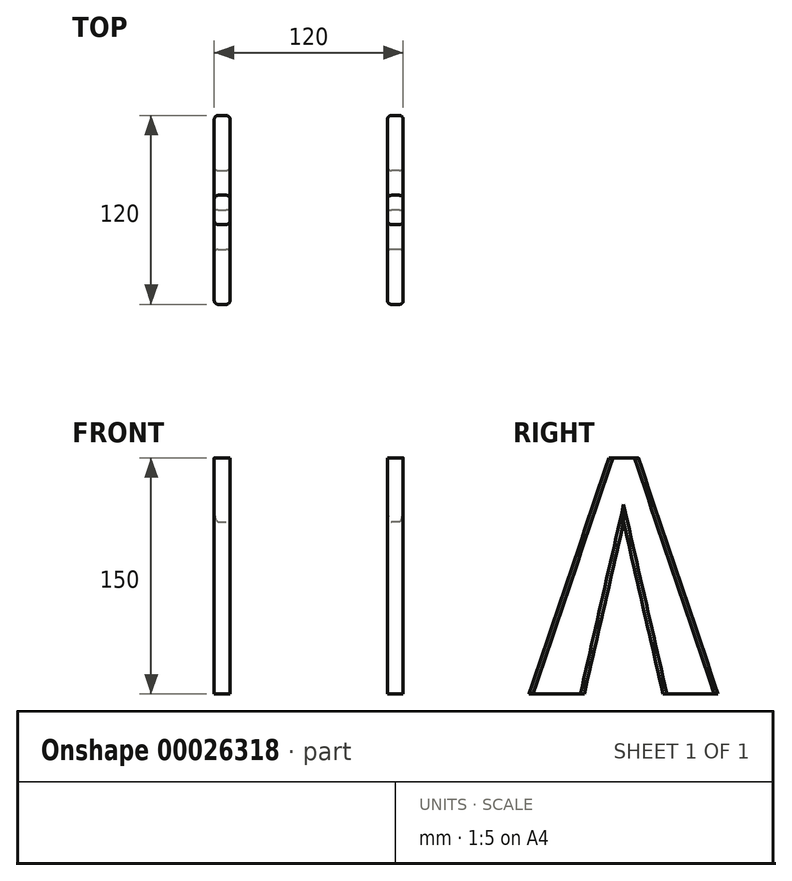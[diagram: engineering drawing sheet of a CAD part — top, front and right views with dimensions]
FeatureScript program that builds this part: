
annotation { "Feature Type Name" : "Feature", "Feature Type Description" : "" }
export const myFeature = defineFeature(function(context is Context, id is Id, definition is map)
    precondition{}
    {
        {
            var Q0;
            Q0=qCreatedBy(makeId("Top.planeOp"),FACE);
            var sketch = newSketch(context, id + "F0", { "sketchPlane" : qUnion([Q0])});
            skLineSegment(sketch, "E0.bottom", {"start": v(-57.5, -25) * mm, "end": v(-52.5, -25) * mm});
            skLineSegment(sketch, "E0.top", {"start": v(-57.5, -60) * mm, "end": v(-52.5, -60) * mm});
            skLineSegment(sketch, "E0.left", {"start": v(-60, -27.5) * mm, "end": v(-60, -57.5) * mm});
            skLineSegment(sketch, "E0.right", {"start": v(-50, -27.5) * mm, "end": v(-50, -57.5) * mm});
            skLineSegment(sketch, "E1.MirrorCS", {"start": v(-57.5, 25) * mm, "end": v(-52.5, 25) * mm});
            skLineSegment(sketch, "E2.MirrorCS", {"start": v(-57.5, 60) * mm, "end": v(-52.5, 60) * mm});
            skLineSegment(sketch, "E3.MirrorCS", {"start": v(-50, 27.5) * mm, "end": v(-50, 57.5) * mm});
            skLineSegment(sketch, "E4.MirrorCS", {"start": v(-60, 27.5) * mm, "end": v(-60, 57.5) * mm});
            skPoint(sketch, "E5.visualSharp", {"position": v(-60, -60) * mm});
            skArc(sketch, "E5.filletArc", {"start": v(-60, -57.5) * mm, "mid": v(-59.27, -59.27) * mm, "end": v(-57.5, -60) * mm});
            skPoint(sketch, "E6.visualSharp", {"position": v(-50, -25) * mm});
            skArc(sketch, "E6.filletArc", {"start": v(-50, -27.5) * mm, "mid": v(-50.73, -25.73) * mm, "end": v(-52.5, -25) * mm});
            skPoint(sketch, "E7.visualSharp", {"position": v(-60, -25) * mm});
            skArc(sketch, "E7.filletArc", {"start": v(-57.5, -25) * mm, "mid": v(-59.27, -25.73) * mm, "end": v(-60, -27.5) * mm});
            skPoint(sketch, "E8.visualSharp", {"position": v(-50, -60) * mm});
            skArc(sketch, "E8.filletArc", {"start": v(-52.5, -60) * mm, "mid": v(-50.73, -59.27) * mm, "end": v(-50, -57.5) * mm});
            skPoint(sketch, "E9.visualSharp", {"position": v(-50, 25) * mm});
            skArc(sketch, "E9.filletArc", {"start": v(-52.5, 25) * mm, "mid": v(-50.73, 25.73) * mm, "end": v(-50, 27.5) * mm});
            skPoint(sketch, "E10.visualSharp", {"position": v(-60, 25) * mm});
            skArc(sketch, "E10.filletArc", {"start": v(-60, 27.5) * mm, "mid": v(-59.27, 25.73) * mm, "end": v(-57.5, 25) * mm});
            skPoint(sketch, "E11.visualSharp", {"position": v(-60, 60) * mm});
            skArc(sketch, "E11.filletArc", {"start": v(-57.5, 60) * mm, "mid": v(-59.27, 59.27) * mm, "end": v(-60, 57.5) * mm});
            skPoint(sketch, "E12.visualSharp", {"position": v(-50, 60) * mm});
            skArc(sketch, "E12.filletArc", {"start": v(-50, 57.5) * mm, "mid": v(-50.73, 59.27) * mm, "end": v(-52.5, 60) * mm});
            skSolve(sketch);
        }
        {
            var Q0;
            Q0=qCreatedBy(makeId("Top.planeOp"),FACE);
            cPlane(context, id + "F1", {"entities" : qUnion([Q0]), "cplaneType" : CPlaneType.OFFSET, "offset" : 150 * mm, "width" : 150 * mm, "height" : 150 * mm});
        }
        {
            var Q0;
            Q0=qCreatedBy(id+"F1.planeOp",FACE);
            var sketch = newSketch(context, id + "F2", { "sketchPlane" : qUnion([Q0])});
            skLineSegment(sketch, "E13.rect.bottom", {"start": v(-57.5, 9.3) * mm, "end": v(-52.5, 9.3) * mm});
            skLineSegment(sketch, "E13.rect.top", {"start": v(-57.5, -9.3) * mm, "end": v(-52.5, -9.3) * mm});
            skLineSegment(sketch, "E13.rect.left", {"start": v(-60, 6.8) * mm, "end": v(-60, -6.8) * mm});
            skLineSegment(sketch, "E13.rect.right", {"start": v(-50, 6.8) * mm, "end": v(-50, -6.8) * mm});
            skPoint(sketch, "E13.rect.middle", {"position": v(-55, 0) * mm});
            skLineSegment(sketch, "E14", {"start": v(-55, 0) * mm, "end": v(-55, 25) * mm, "construction": true});
            skLineSegment(sketch, "E15", {"start": v(-55, 25) * mm, "end": v(-55, 0) * mm, "construction": true});
            skLineSegment(sketch, "E16", {"start": v(-55, 0) * mm, "end": v(-55, -25) * mm, "construction": true});
            skPoint(sketch, "E17.visualSharp", {"position": v(-60, 9.3) * mm});
            skArc(sketch, "E17.filletArc", {"start": v(-57.5, 9.3) * mm, "mid": v(-59.27, 8.56) * mm, "end": v(-60, 6.8) * mm});
            skPoint(sketch, "E18.visualSharp", {"position": v(-50, 9.3) * mm});
            skArc(sketch, "E18.filletArc", {"start": v(-50, 6.8) * mm, "mid": v(-50.73, 8.56) * mm, "end": v(-52.5, 9.3) * mm});
            skPoint(sketch, "E19.visualSharp", {"position": v(-50, -9.3) * mm});
            skArc(sketch, "E19.filletArc", {"start": v(-52.5, -9.3) * mm, "mid": v(-50.73, -8.56) * mm, "end": v(-50, -6.8) * mm});
            skPoint(sketch, "E20.visualSharp", {"position": v(-60, -9.3) * mm});
            skArc(sketch, "E20.filletArc", {"start": v(-60, -6.8) * mm, "mid": v(-59.27, -8.56) * mm, "end": v(-57.5, -9.3) * mm});
            skSolve(sketch);
        }
        {
            var Q0;
            Q0=makeQuery(id+"F0.imprint","IMPRINT",FACE,{"disambiguationData":[TD([[makeQuery(id+"F0.imprint","IMPRINT",EDGE,{"derivedFrom":sQuery(id+"F0.wireOp",EDGE,"E0.bottom")}),-1.0]])]});
            var Q1;
            Q1=makeQuery(id+"F2.imprint","IMPRINT",FACE,{"disambiguationData":[TD([[makeQuery(id+"F2.imprint","IMPRINT",EDGE,{"derivedFrom":sQuery(id+"F2.wireOp",EDGE,"E13.rect.bottom")}),-1.0]])]});
            loft(context, id + "F3", {"sheetProfilesArray" : [{ "sheetProfileEntities" : qUnion([Q0]) }, { "sheetProfileEntities" : qUnion([Q1]) }]});
        }
        {
            var Q1;
            Q1=makeQuery(id+"F0.imprint","IMPRINT",FACE,{"disambiguationData":[TD([[makeQuery(id+"F0.imprint","IMPRINT",EDGE,{"derivedFrom":sQuery(id+"F0.wireOp",EDGE,"E1.MirrorCS")}),1.0]])]});
            var Q2;
            Q2=makeQuery(id+"F2.imprint","IMPRINT",FACE,{"disambiguationData":[TD([[makeQuery(id+"F2.imprint","IMPRINT",EDGE,{"derivedFrom":sQuery(id+"F2.wireOp",EDGE,"E13.rect.bottom")}),-1.0]])]});
            loft(context, id + "F4", {"operationType" : NewBodyOperationType.ADD, "sheetProfilesArray" : [{ "sheetProfileEntities" : qUnion([Q1]) }, { "sheetProfileEntities" : qUnion([Q2]) }]});
        }
        {
            var Q0;
            Q0=makeQuery(id+"F3.opLoft","SWEPT_BODY",BODY,{"disambiguationData":[OSD([makeQuery(id+"F0.imprint","IMPRINT",FACE,{"disambiguationData":[TD([[makeQuery(id+"F0.imprint","IMPRINT",EDGE,{"derivedFrom":sQuery(id+"F0.wireOp",EDGE,"E0.bottom")}),-1.0]])]}),makeQuery(id+"F2.imprint","IMPRINT",FACE,{"disambiguationData":[TD([[makeQuery(id+"F2.imprint","IMPRINT",EDGE,{"derivedFrom":sQuery(id+"F2.wireOp",EDGE,"E13.rect.bottom")}),-1.0]])]})])]});
            var Q1;
            Q1=qCreatedBy(makeId("Right.planeOp"),FACE);
            mirror(context, id + "F5", {"entities" : qUnion([Q0]), "mirrorPlane" : qUnion([Q1])});
        }
    });
